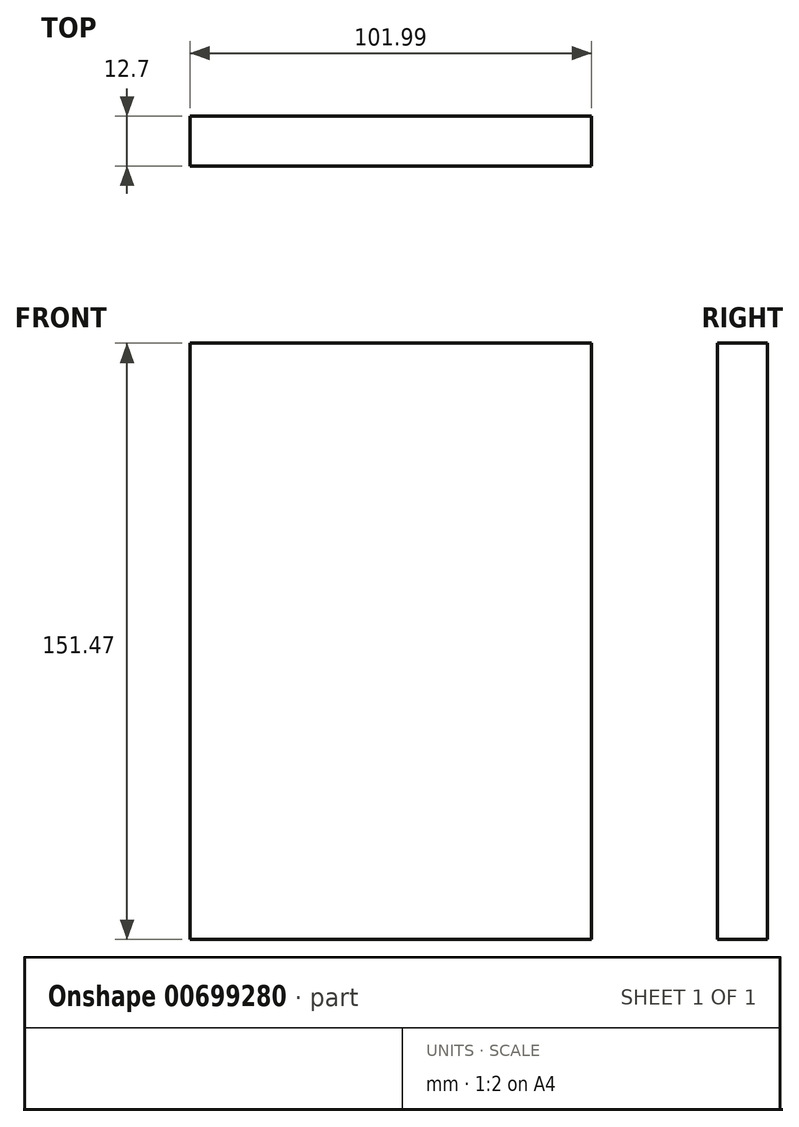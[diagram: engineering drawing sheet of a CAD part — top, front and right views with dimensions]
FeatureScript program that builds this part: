
annotation { "Feature Type Name" : "Feature", "Feature Type Description" : "" }
export const myFeature = defineFeature(function(context is Context, id is Id, definition is map)
    precondition{}
    {
        {
            var Q0;
            Q0=qCreatedBy(makeId("Front.planeOp"),FACE);
            var sketch = newSketch(context, id + "F0", { "sketchPlane" : qUnion([Q0])});
            skLineSegment(sketch, "E0.bottom", {"start": v(48.4, 75.58) * mm, "end": v(-53.6, 75.58) * mm});
            skLineSegment(sketch, "E0.top", {"start": v(48.4, -75.89) * mm, "end": v(-53.6, -75.89) * mm});
            skLineSegment(sketch, "E0.left", {"start": v(48.4, 75.58) * mm, "end": v(48.4, -75.89) * mm});
            skLineSegment(sketch, "E0.right", {"start": v(-53.6, 75.58) * mm, "end": v(-53.6, -75.89) * mm});
            skSolve(sketch);
        }
        {
            var Q0;
            Q0=makeQuery(id+"F0.imprint","IMPRINT",FACE,{"disambiguationData":[TD([[makeQuery(id+"F0.imprint","IMPRINT",EDGE,{"derivedFrom":sQuery(id+"F0.wireOp",EDGE,"E0.bottom")}),1.0]])]});
            extrude(context, id + "F1", {"entities" : qUnion([Q0]), "depth" : 12.7 * mm, "offsetDistance" : 25.4 * mm});
        }
    });
